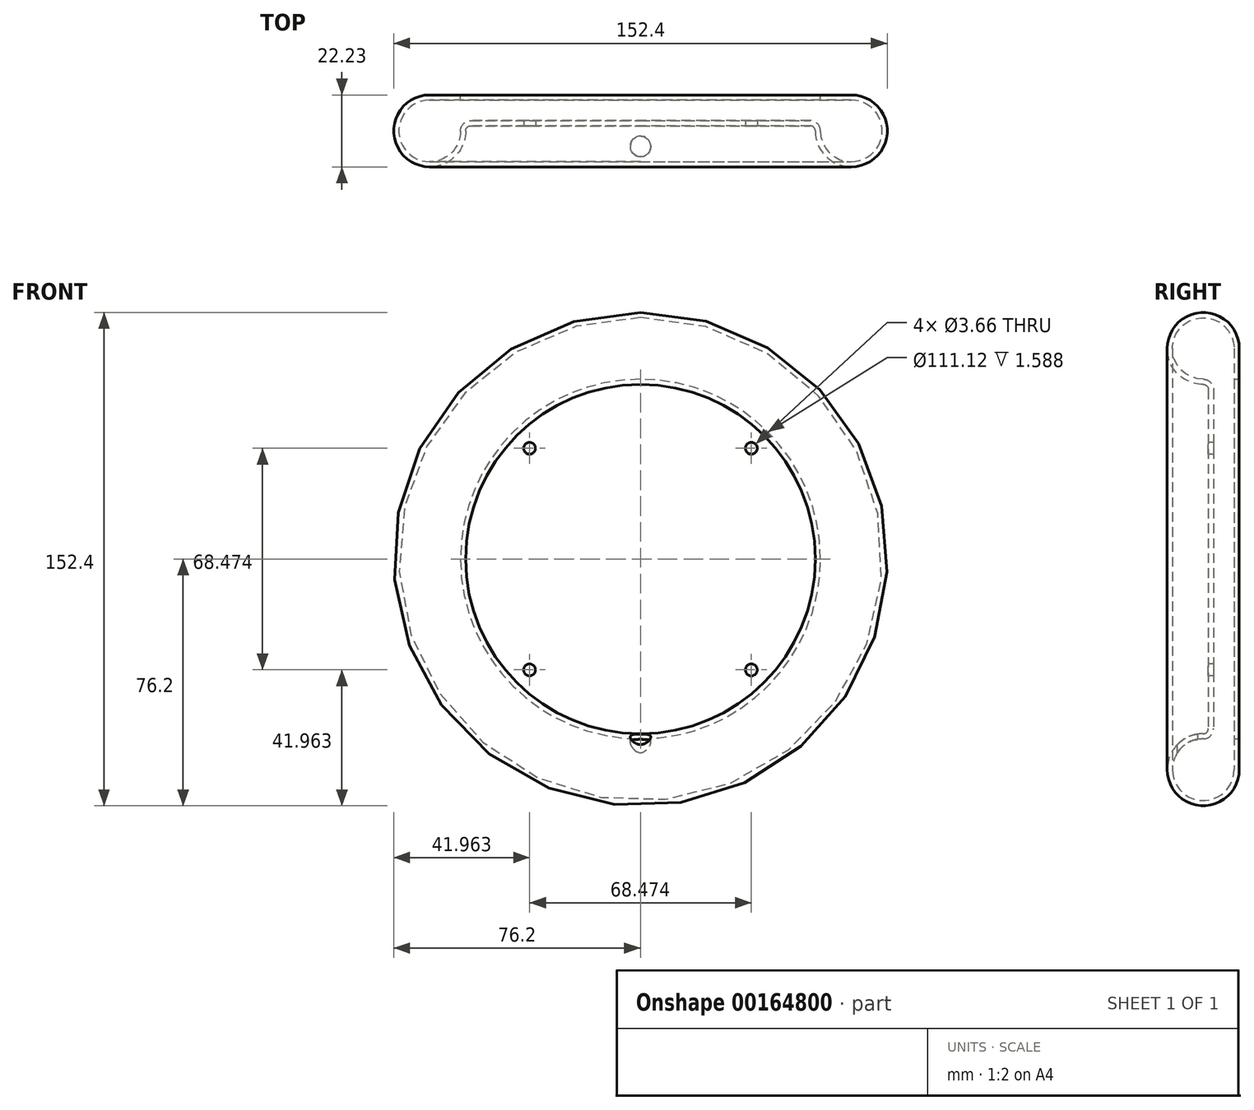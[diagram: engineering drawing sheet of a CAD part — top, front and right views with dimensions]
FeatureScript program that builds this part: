
annotation { "Feature Type Name" : "Feature", "Feature Type Description" : "" }
export const myFeature = defineFeature(function(context is Context, id is Id, definition is map)
    precondition{}
    {
        {
            var Q0;
            Q0=qCreatedBy(makeId("Top.planeOp"),FACE);
            var sketch = newSketch(context, id + "F0", { "sketchPlane" : qUnion([Q0])});
            skLineSegment(sketch, "E0", {"start": v(0, 0) * mm, "end": v(65.09, 0) * mm});
            skLineSegment(sketch, "E1", {"start": v(0, 0) * mm, "end": v(0, 1.59) * mm});
            skArc(sketch, "E2", {"start": v(55.56, -9.52) * mm, "mid": v(71.82, -16.26) * mm, "end": v(65.09, 0) * mm});
            skLineSegment(sketch, "E3", {"start": v(0, 1.59) * mm, "end": v(65.09, 1.59) * mm});
            skLineSegment(sketch, "E4", {"start": v(65.09, 0) * mm, "end": v(65.09, 1.59) * mm, "construction": true});
            skLineSegment(sketch, "E5", {"start": v(0, 0) * mm, "end": v(0, -6.35) * mm, "construction": true});
            skLineSegment(sketch, "E6.bottom", {"start": v(0, -6.35) * mm, "end": v(52.39, -6.35) * mm});
            skLineSegment(sketch, "E6.top", {"start": v(0, -7.94) * mm, "end": v(52.39, -7.94) * mm});
            skLineSegment(sketch, "E6.left", {"start": v(0, -6.35) * mm, "end": v(0, -7.94) * mm});
            skLineSegment(sketch, "E6.right", {"start": v(52.39, -6.35) * mm, "end": v(52.39, -7.94) * mm});
            skArc(sketch, "E7", {"start": v(55.56, -9.52) * mm, "mid": v(54.63, -7.28) * mm, "end": v(52.39, -6.35) * mm});
            skArc(sketch, "E8", {"start": v(53.98, -9.52) * mm, "mid": v(53.51, -8.4) * mm, "end": v(52.39, -7.94) * mm});
            skArc(sketch, "E9", {"start": v(53.98, -9.52) * mm, "mid": v(72.95, -17.38) * mm, "end": v(65.09, 1.59) * mm});
            skLineSegment(sketch, "E10", {"start": v(0, -7.94) * mm, "end": v(0, -20.64) * mm, "construction": true});
            skLineSegment(sketch, "E11", {"start": v(0, -20.64) * mm, "end": v(65.09, -20.64) * mm, "construction": true});
            skLineSegment(sketch, "E12", {"start": v(65.09, -9.52) * mm, "end": v(65.09, -6.35) * mm, "construction": true});
            skLineSegment(sketch, "E13", {"start": v(65.09, -6.35) * mm, "end": v(52.39, -6.35) * mm, "construction": true});
            skSolve(sketch);
        }
        {
            var Q0;
            Q0=qCreatedBy(makeId("Front.planeOp"),FACE);
            var sketch = newSketch(context, id + "F1", { "sketchPlane" : qUnion([Q0])});
            skCircle(sketch, "E14", {"center": v(0, 0) * mm, "radius": 12.7 * mm});
            skSolve(sketch);
        }
        {
            var Q0;
            Q0=makeQuery(id+"F0.imprint","IMPRINT",FACE,{"disambiguationData":[TD([[makeQuery(id+"F0.imprint","IMPRINT",EDGE,{"derivedFrom":sQuery(id+"F0.wireOp",EDGE,"E0")}),1.0]])]});
            var Q1;
            Q1=makeQuery(id+"F0.imprint","IMPRINT",FACE,{"disambiguationData":[TD([[makeQuery(id+"F0.imprint","IMPRINT",EDGE,{"derivedFrom":sQuery(id+"F0.wireOp",EDGE,"E6.bottom")}),-1.0]])]});
            var Q2;
            Q2=sQuery(id+"F1.wireOp",EDGE,"E14");
            revolve(context, id + "F2", {"entities" : qUnion([Q0, Q1]), "axis" : qUnion([Q2]), "revolveType" : RevolveType.FULL});
        }
        {
            var Q0;
            Q0=makeQuery(id+"F2.opRevolve","SWEPT_FACE",FACE,{"disambiguationData":[OSD([sQuery(id+"F0.wireOp",EDGE,"E3")])]});
            var sketch = newSketch(context, id + "F3", { "sketchPlane" : qUnion([Q0])});
            skCircle(sketch, "E15", {"center": v(0, 0) * mm, "radius": 55.56 * mm});
            skSolve(sketch);
        }
        {
            var Q0;
            Q0 = qSketchRegion(id + "F3", true);
            extrude(context, id + "F4", {"entities" : qUnion([Q0]), "operationType" : NewBodyOperationType.REMOVE, "oppositeDirection" : true, "depth" : 1.59 * mm});
        }
        {
            var Q0;
            Q0=qCreatedBy(makeId("Top.planeOp"),FACE);
            var sketch = newSketch(context, id + "F5", { "sketchPlane" : qUnion([Q0])});
            skLineSegment(sketch, "E16", {"start": v(0, -7.94) * mm, "end": v(0, -14.29) * mm, "construction": true});
            skCircle(sketch, "E17", {"center": v(0, -14.29) * mm, "radius": 3.18 * mm});
            skSolve(sketch);
        }
        {
            var Q0;
            Q0 = qSketchRegion(id + "F5", true);
            var Q1;
            Q1=makeQuery(id+"F2.opRevolve","SWEPT_FACE",FACE,{"disambiguationData":[OSD([sQuery(id+"F0.wireOp",EDGE,"E2")])]});
            extrude(context, id + "F6", {"entities" : qUnion([Q0]), "operationType" : NewBodyOperationType.REMOVE, "endBound" : BoundingType.UP_TO_SURFACE, "oppositeDirection" : true, "endBoundEntityFace" : qUnion([Q1]), "depth" : 25.4 * mm});
        }
        {
            var Q0;
            Q0=makeQuery(id+"F2.opRevolve","SWEPT_FACE",FACE,{"disambiguationData":[OSD([sQuery(id+"F0.wireOp",EDGE,"E6.top")])]});
            var sketch = newSketch(context, id + "F7", { "sketchPlane" : qUnion([Q0])});
            skCircle(sketch, "E18", {"center": v(34.24, -34.24) * mm, "radius": 3.97 * mm, "construction": true});
            skLineSegment(sketch, "E19.bottom", {"start": v(34.24, -34.24) * mm, "end": v(-34.24, -34.24) * mm, "construction": true});
            skLineSegment(sketch, "E19.top", {"start": v(34.24, 34.24) * mm, "end": v(-34.24, 34.24) * mm, "construction": true});
            skLineSegment(sketch, "E19.left", {"start": v(34.24, -34.24) * mm, "end": v(34.24, 34.24) * mm, "construction": true});
            skLineSegment(sketch, "E19.right", {"start": v(-34.24, -34.24) * mm, "end": v(-34.24, 34.24) * mm, "construction": true});
            skPoint(sketch, "E19.middle", {"position": v(0, 0) * mm});
            skCircle(sketch, "E20", {"center": v(34.24, -34.24) * mm, "radius": 1.83 * mm});
            skCircle(sketch, "E21", {"center": v(-34.24, -34.24) * mm, "radius": 1.83 * mm});
            skCircle(sketch, "E22", {"center": v(-34.24, 34.24) * mm, "radius": 1.83 * mm});
            skCircle(sketch, "E23", {"center": v(34.24, 34.24) * mm, "radius": 1.83 * mm});
            skSolve(sketch);
        }
        {
            var Q0;
            Q0 = qSketchRegion(id + "F7", true);
            var Q1;
            Q1=makeQuery(id+"F2.opRevolve","SWEPT_FACE",FACE,{"disambiguationData":[OSD([sQuery(id+"F0.wireOp",EDGE,"E6.bottom")])]});
            extrude(context, id + "F8", {"entities" : qUnion([Q0]), "operationType" : NewBodyOperationType.REMOVE, "endBound" : BoundingType.UP_TO_SURFACE, "oppositeDirection" : true, "endBoundEntityFace" : qUnion([Q1]), "depth" : 25.4 * mm});
        }
    });
